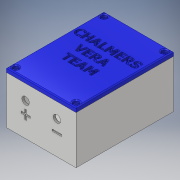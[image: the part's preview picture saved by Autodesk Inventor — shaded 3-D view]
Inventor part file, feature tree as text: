
AUTODESK INVENTOR PART (.ipt)
format: ipt  version: 2019.3 (Build 233278000, 278)  size: 1,969,152 bytes
history: native  units: mm
features: sketch x11, extrude x10, chamfer x3, plane x1, mirror x1, hole x1
ambient origin geometry x8: Origin, YZ Plane, XZ Plane, XY Plane, X Axis, Y Axis, Z Axis, Center Point
bodies: Solid1 (feature_tree), Solid2 (feature_tree)
feature tree (27):
  sketch  "Sketch1"  dims[d0=100.0mm d1=70.0mm]
  extrude  "Extrusion1"  Depth=70.0mm
  extrude  "Extrusion2"  Depth=2.4mm
  extrude  "Extrusion3"  TaperAngle=0.0deg  [1 undecoded]
  extrude  "Extrusion4"  TaperAngle=0.0deg  [1 undecoded]
  extrude  "Extrusion5"  Depth=16.0mm
  extrude  "Extrusion6"  TaperAngle=0.0deg  [1 undecoded]
  plane  "Work Plane1"
  mirror  "Mirror1"
  extrude  "Extrusion7"  Depth=3.0mm TaperAngle=0.0deg
  sketch  "Sketch8"  dims[d12=12.0mm d13=3.0mm d14=0.0mm]
  extrude  "Extrusion8"  Depth=7.0mm
  chamfer  "Chamfer1"  Distance=30.0mm
  extrude  "Extrusion9"  TaperAngle=0.0deg  [1 undecoded]
  hole  "Hole1"  [1 undecoded]
  chamfer  "Chamfer2"  Distance=10.0mm
  chamfer  "Chamfer3"  Distance=2.0mm
  extrude  "Extrusion10"  Depth=2.4mm
  sketch  "Sketch2"  dims[d2=2.4mm d3=2.4mm]
  sketch  "Sketch3"  dims[d4=50.0mm d5=0.0mm]
  sketch  "Sketch5"  dims[d6=2.4mm d7=0.0mm]
  sketch  "Sketch6"  dims[d8=8.0mm d9=16.0mm]
  sketch  "Sketch7"  dims[d10=2.4mm d11=0.0mm]
  sketch  "Sketch9"  dims[d15=6.0mm d16=7.0mm]
  sketch  "Sketch10"  dims[d17=10.0mm]
  sketch  "Sketch11"  dims[d18=4.0mm]
  sketch  "Sketch12"  dims[d20=15.0mm d21=30.0mm d22=0.0mm d23=0.0mm d24=2.0mm d25=10.0mm d26=2.0mm d27=2.0mm d28=10.0mm d29=10.0mm d30=1.2mm d31=0.0mm d32=8.0mm d33=1.2mm d34=0.0mm d35=5.0mm d36=5.0mm d37=10.0mm d38=0.0mm d39=5.0mm d40=2.0mm d41=45.0deg d42=4.8mm d43=0.0mm d44=45.0deg d45=3.0mm d46=6.0mm d47=6.0mm d48=3.0mm d49=90.0deg d50=8.0mm d51=20.594885mm d52=1.0mm d53=2.0mm d54=45.0deg d55=5.0mm d56=2.0mm d57=45.0deg d58=2.4mm d59=0.0mm]
note: 5 required parameter values undecoded (feature->parameter linkage not recoverable at this tier; creation-order binding heuristic only, values carry confidence <= 0.55)
